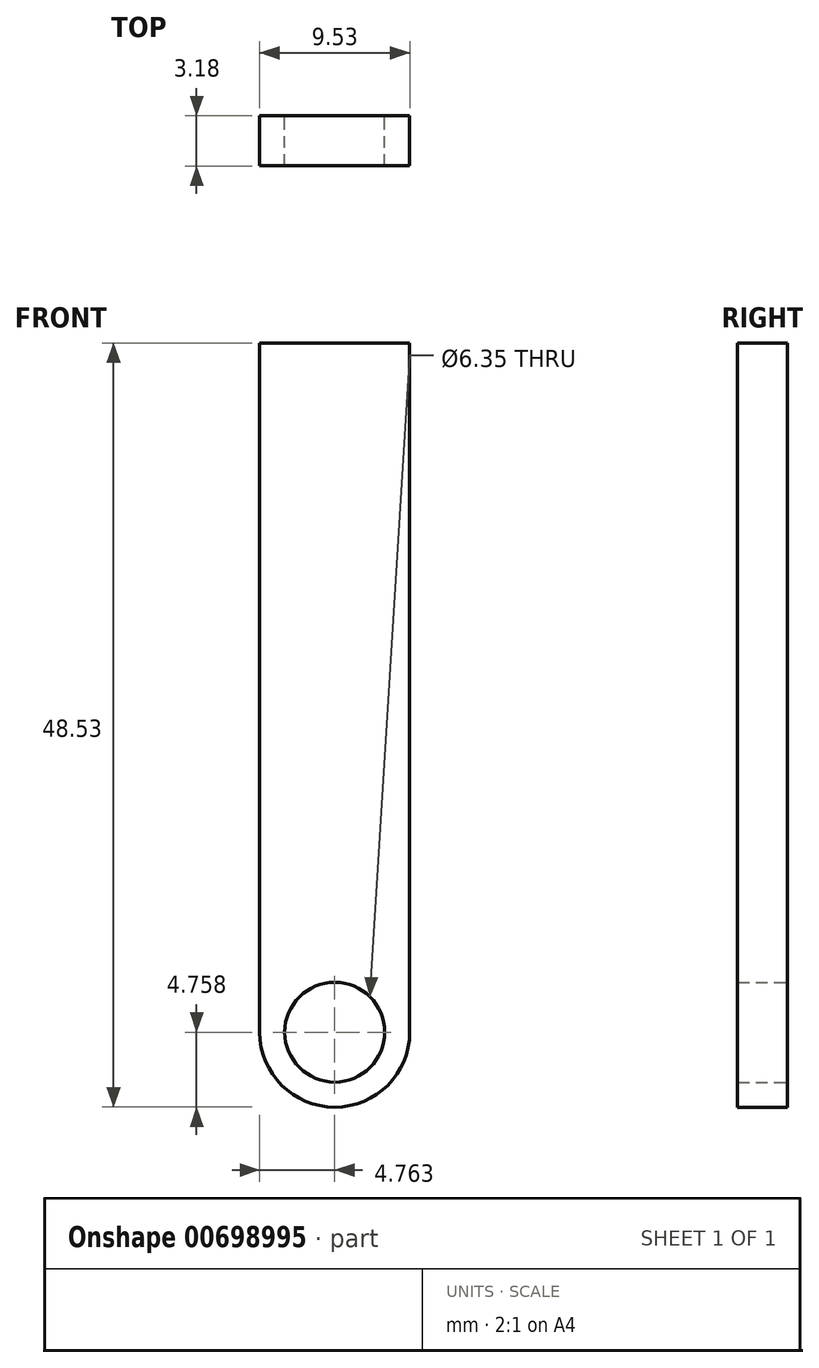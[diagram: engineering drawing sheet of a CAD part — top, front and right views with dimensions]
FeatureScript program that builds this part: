
annotation { "Feature Type Name" : "Feature", "Feature Type Description" : "" }
export const myFeature = defineFeature(function(context is Context, id is Id, definition is map)
    precondition{}
    {
        {
            var Q0;
            Q0=qCreatedBy(makeId("Front.planeOp"),FACE);
            var sketch = newSketch(context, id + "F0", { "sketchPlane" : qUnion([Q0])});
            skLineSegment(sketch, "E0", {"start": v(0, 0) * mm, "end": v(0, -45.35) * mm});
            skLineSegment(sketch, "E1", {"start": v(0, 0) * mm, "end": v(0, 3.18) * mm});
            skLineSegment(sketch, "E2", {"start": v(0, 3.18) * mm, "end": v(9.53, 3.18) * mm});
            skLineSegment(sketch, "E3", {"start": v(9.53, 3.18) * mm, "end": v(9.53, -45.35) * mm});
            skLineSegment(sketch, "E4", {"start": v(0, -45.35) * mm, "end": v(9.52, -45.35) * mm});
            skPoint(sketch, "E5", {"position": v(4.76, -45.35) * mm});
            skLineSegment(sketch, "E6", {"start": v(4.76, -45.35) * mm, "end": v(4.76, -40.6) * mm});
            skCircle(sketch, "E7", {"center": v(4.76, -40.6) * mm, "radius": 3.18 * mm});
            skSolve(sketch);
        }
        {
            var Q0;
            {var subQ1=sQuery(id+"F0.wireOp",EDGE,"E0");Q0=makeQuery(id+"F0.imprint","IMPRINT",FACE,{"disambiguationData":[TD([[makeQuery(id+"F0.imprint","IMPRINT",EDGE,{"derivedFrom":subQ1}),1.0]])]});}
            extrude(context, id + "F1", {"entities" : qUnion([Q0]), "depth" : 3.17 * mm, "offsetDistance" : 25.4 * mm});
        }
        {
            var Q0;
            Q0=makeQuery(id+"F1.opExtrude","SWEPT_EDGE",EDGE,{"disambiguationData":[OSD([sQuery(id+"F0.wireOp",EDGE,"E0"),sQuery(id+"F0.wireOp",EDGE,"E4")])]});
            var Q1;
            Q1=makeQuery(id+"F1.opExtrude","SWEPT_EDGE",EDGE,{"disambiguationData":[OSD([sQuery(id+"F0.wireOp",EDGE,"E3"),sQuery(id+"F0.wireOp",EDGE,"E4")])]});
            fillet(context, id + "F2", {"entities" : qUnion([Q0, Q1]), "radius" : 4.76 * mm, "tangentPropagation" : true, "allowEdgeOverflow" : false});
        }
    });
